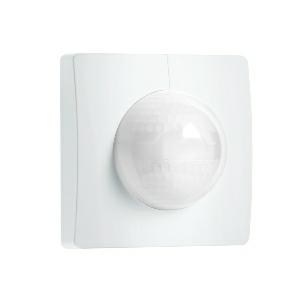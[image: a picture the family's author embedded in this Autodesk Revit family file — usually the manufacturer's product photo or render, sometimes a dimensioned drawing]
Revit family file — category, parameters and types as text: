
# Revit family: is_3180_055721
name_source: partatom
category: Elektroinstallationen
revit_build: Autodesk Revit 2016 (Build: 20190508_0715(x64)
units: mm (PartAtom-declared; Revit-internal decimal feet)

## family parameters
Basisbauteil = Fläche
Beim Laden mit Abzugskörper schneiden = Nein
Bemaßung runder Anschluss = Durchmesser verwenden
Beschriftungsausrichtung beibehalten = Nein
Gemeinsam genutzt = Nein
Raumberechnungspunkt = Nein
Teiletyp = Normal

## types (1)
- IS 3180
    Apparent Load = 0 VA
    Beschreibung = Type: Motion detectors; Dimensions (L x W x H): 78 x 94 x 94 mm; Mains power supply: 220 – 240 V / 50 – 60 Hz; Sensor Technology: passive infrared; Application, place: Indoors; Application, room: corridor / aisle, function room / ancillary room, stairwell, multi-storey / underground car park, outdoors, all round the building, courtyard & driveway, Indoors; Installation site: wall, corner; Installation: Concealed wiring; Switching zones: 448 switching zones; Electronic scalability: No; Mounting height: 1,80 – 2,50 m; Optimum mounting height: 2 m; Detection angle: 180 °; Angle of aperture: 90 °; Sneak-by guard: Yes; Reach, radial: r = 4 m (25 m²); Reach, tangential: r = 20 m (628 m²); Twilight setting TEACH: Yes; Twilight setting: 2 – 1000 lx; Time setting: 5 sec – 15 min; Switching output 1, resistive: 2000 W; Switching output 1, number of LEDs / fluorescent lamps: 8 pcs.; Constant-lighting control: No; Basic light level function: No; Functions: Normal / test mode, Manual ON / ON-OFF; Settings via: Remote control, Potentiometers, Smart Remote; With remote control: No; Interconnection: Yes; IP-rating: IP20; Material: Plastic; Ambient temperature: -20 – 50 °C; Colour: white; Colour, RAL: 9003; Manufacturer's Warranty: 5 years; Version: COM1 - concealed, sq.; PU1, EAN: 4007841055721
    Height = 94 mm  [stored 0.308399 ft]
    Hersteller = Steinel
    Length = 78 mm  [stored 0.255906 ft]
    Maximum range = 22.153 m
    ModVariant = Nein
    Modell = 055721
    Mounting Type = Recessed
    Number of Poles = 1
    OnlyDefault = Ja
    Power Factor = 1
    Product Name = IS 3180
    Product group = Sensor-switched indoor light
    ProductGroupID = 30
    Protection Class = Protection class
    Protection Degree = IP 20
    RlxData = <blob elided: 167821 chars, md5=aafbd9e5>
    Sensor characteristics = Semi circular 145°-300°
    Sensor type = Passive (infrared)
    SensorDataFile = <blob elided: 5082 chars, md5=d953030a>
    Type of entry = Motion
    Typenbild = produkt1_055721.jpg
    Typenkommentare = Product without accessories
    URL = http://relux.com
    VarID = ---
    Voltage = 0 V
    Vorgabe-Ansicht = 1800 mm
    Weight = 0.00 kg
    Width = 94 mm  [stored 0.308399 ft]

note: [stored X ft] marks values corroborated as IEEE doubles in the binary element streams (Revit-internal decimal feet)

## geometry (parser evidence)
native form markers: Sweep x18
no freeform markers — native parametric forms only
